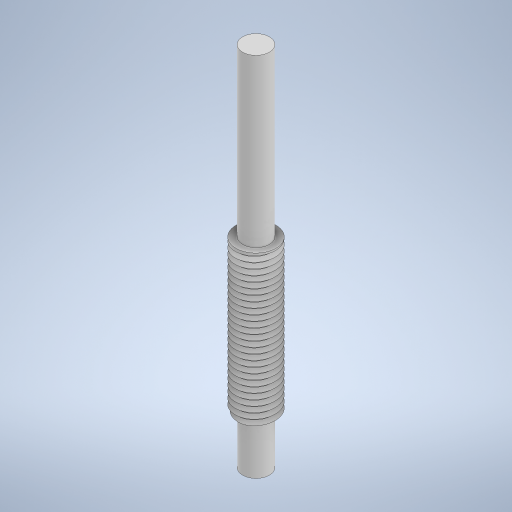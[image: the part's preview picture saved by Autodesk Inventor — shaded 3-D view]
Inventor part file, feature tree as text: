
AUTODESK INVENTOR PART (.ipt)
format: ipt  version: 2024 (Build 280153000, 153)  size: 621,568 bytes
history: native  units: mm
features: sketch x6, extrude x3, helix x1
ambient origin geometry x8: Origin, YZ Plane, XZ Plane, XY Plane, X Axis, Y Axis, Z Axis, Center Point
bodies: Solid1 (feature_tree)
feature tree (10):
  sketch  "Sketch1"  dims[d0=12.0mm d1=45.0mm d2=0.0mm d3=1.7mm]
  extrude  "Extrusion1"  Depth=45.0mm TaperAngle=0.0deg
  helix  "Coil1"  [1 undecoded]
  extrude  "Extrusion2"  Depth=0.2mm
  extrude  "Extrusion3"  Depth=10.0mm
  sketch  "Sketch2"  dims[d4=60.0deg d5=0.2mm]
  sketch  "Sketch3"  dims[d6=0.1mm]
  sketch  "Sketch4"  dims[d7=1.7mm d8=45.0mm d9=10.0mm d10=0.0mm d11=90.0deg d12=90.0deg d13=0.0mm d14=0.0mm d15=8.0mm]
  sketch  "Sketch5"  dims[d16=50.0mm d17=0.0mm]
  sketch  "Sketch6"  dims[d18=8.0mm d19=15.0mm d20=0.0mm]
note: 1 required parameter value undecoded (feature->parameter linkage not recoverable at this tier; creation-order binding heuristic only, values carry confidence <= 0.55)
